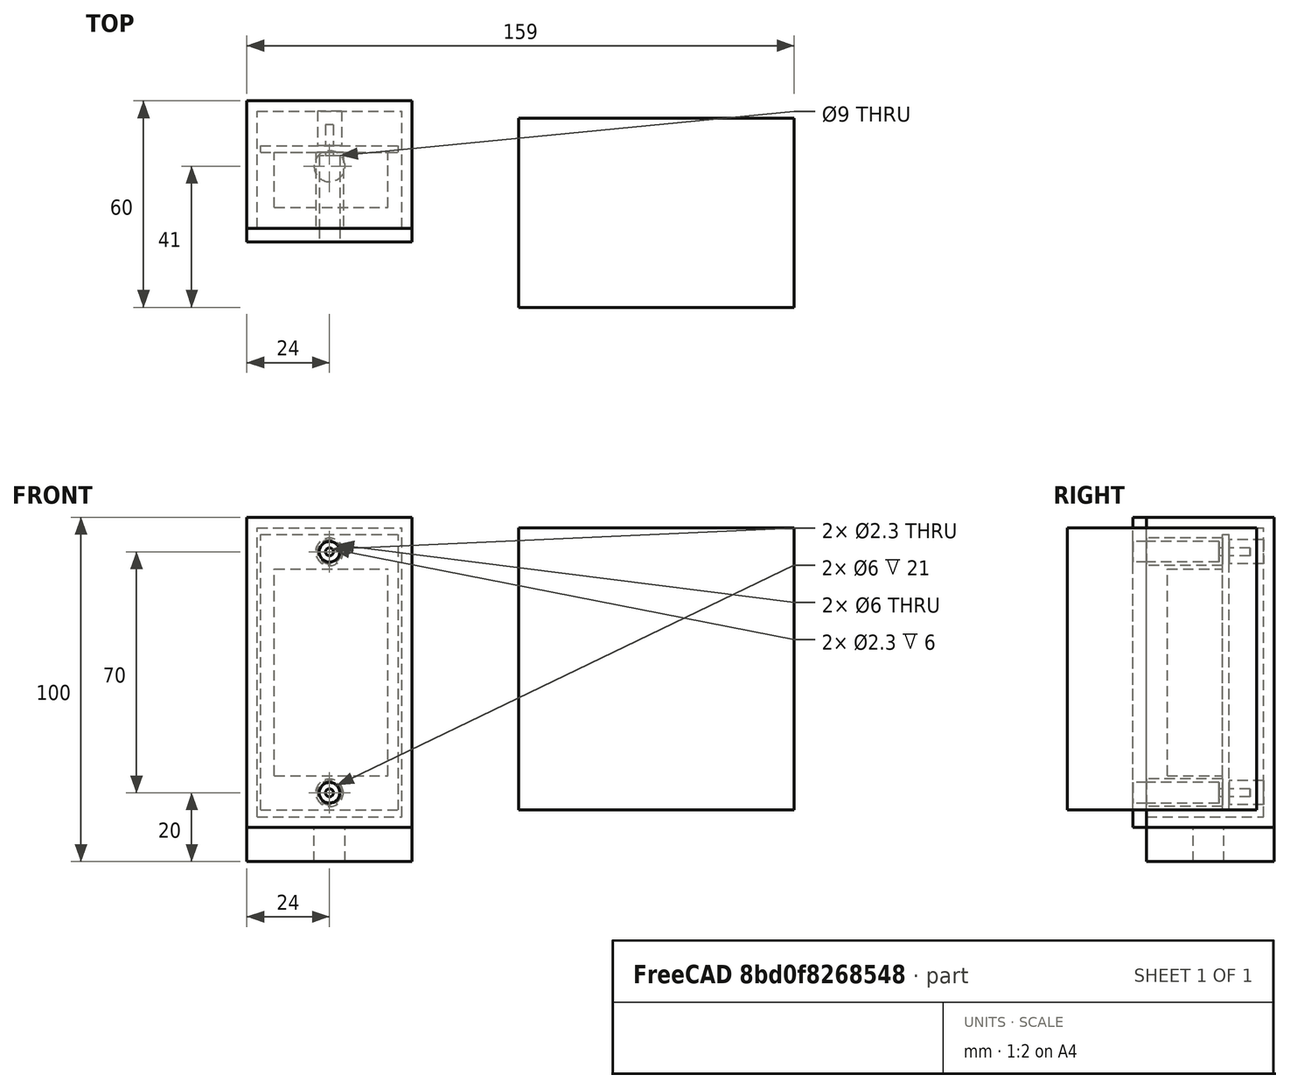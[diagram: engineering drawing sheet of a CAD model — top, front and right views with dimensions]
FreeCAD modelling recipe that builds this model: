
FCSTD DOCUMENT  (FreeCAD 0.15R4671 (Git))
Label: Sense_Beam Basic Enclosure
License: All rights reserved
LicenseURL: http://en.wikipedia.org/wiki/All_rights_reserved
objects: Part::Cylinder×13, Part::MultiFuse×8, Part::Box×7, Part::Cut×6
note: 34 computed .brp shape members not serialized (recipe doc carries the construction recipe); baked Part::Feature solids carry a one-line shape summary decoded from their .brp

FEATURE [Part::Cylinder] Cylinder002  label="PCB Mount1"
  Angle = 360
  Height = 10
  Placement = pos=(0,12,75) rot=(1,0,0;1.5708rad)
  Radius = 3.5
FEATURE [Part::Cylinder] Cylinder003  label="PCB Mount2"
  Angle = 360
  Height = 10
  Placement = pos=(0,12,5) rot=(1,0,0;1.5708rad)
  Radius = 3.5
FEATURE [Part::Cylinder] Cylinder004  label="PCB Mount_cut1"
  Angle = 360
  Height = 6
  Placement = pos=(0,8,75) rot=(1,0,0;1.5708rad)
  Radius = 1.15
FEATURE [Part::Cylinder] Cylinder005  label="PCB Mount_cut2"
  Angle = 360
  Height = 6
  Placement = pos=(0,8,5) rot=(1,0,0;1.5708rad)
  Radius = 1.15
FEATURE [Part::Box] Box  label="PCB"
  Height = 80
  Length = 40
  Placement = pos=(-20,0,0) rot=(0,0,1;0rad)
  Width = 2
FEATURE [Part::Box] Box001  label="AA Battery"
  Height = 60
  Length = 33
  Placement = pos=(-16,-16,10) rot=(0,0,1;0rad)
  Width = 16
FEATURE [Part::Box] Box002  label="G366"
  Height = 82
  Length = 80
  Placement = pos=(55,-45,0) rot=(0,0,1;0rad)
  Width = 55
FEATURE [Part::Cylinder] Cylinder010  label="Back_Mount_cut1"
  Angle = 360
  Height = 22
  Placement = pos=(0,0,75) rot=(1,0,0;1.5708rad)
  Radius = 4
FEATURE [Part::Cylinder] Cylinder011  label="Back_Mount_cut2"
  Angle = 360
  Height = 22
  Placement = pos=(0,0,5) rot=(1,0,0;1.5708rad)
  Radius = 4
FEATURE [Part::Cylinder] Cylinder012  label="PCB Mount_cut2+1"
  Angle = 360
  Height = 6
  Placement = pos=(0,5,5) rot=(1,0,0;1.5708rad)
  Radius = 1.15
FEATURE [Part::Cylinder] Cylinder013  label="PCB Mount_cut1+1"
  Angle = 360
  Height = 6
  Placement = pos=(0,5,75) rot=(1,0,0;1.5708rad)
  Radius = 1.15
FEATURE [Part::MultiFuse] Fusion003
  Shapes = -> [Cylinder004,Cylinder005]
FEATURE [Part::Box] Box003  label="Cube"
  Height = 90
  Length = 48
  Placement = pos=(-24,-22,-5) rot=(0,0,1;0rad)
  Width = 37
FEATURE [Part::Box] Box004  label="Cube001"
  Height = 84
  Length = 42
  Placement = pos=(-21,-22,-2) rot=(0,0,1;0rad)
  Width = 34
FEATURE [Part::Cut] Cut
  Base = -> Box003
  Tool = -> Box004
FEATURE [Part::Box] Box005  label="Back_Cover"
  Height = 90
  Length = 48
  Placement = pos=(-24,-26,-5) rot=(0,0,1;0rad)
  Width = 4
FEATURE [Part::Cylinder] Cylinder  label="PCB Mount_cut1+2"
  Angle = 360
  Height = 22
  Placement = pos=(0,-1,75) rot=(1,0,0;1.5708rad)
  Radius = 3
FEATURE [Part::Cylinder] Cylinder014  label="PCB Mount_cut2+2"
  Angle = 360
  Height = 22
  Placement = pos=(0,-1,5) rot=(1,0,0;1.5708rad)
  Radius = 3
FEATURE [Part::MultiFuse] Fusion
  Shapes = -> [Cylinder013,Cylinder]
FEATURE [Part::MultiFuse] Fusion004
  Shapes = -> [Cylinder012,Cylinder014]
FEATURE [Part::Cut] Cut001  label="Back M 2"
  Base = -> Cylinder011
  Tool = -> Fusion004
FEATURE [Part::Cut] Cut002  label="Back M 1"
  Base = -> Cylinder010
  Tool = -> Fusion
FEATURE [Part::MultiFuse] Fusion005
  Shapes = -> [Cut002,Cut001]
FEATURE [Part::Cylinder] Cylinder015  label="Back_Mount_cut003"
  Angle = 360
  Height = 10
  Placement = pos=(0,-16,75) rot=(1,0,0;1.5708rad)
  Radius = 3
FEATURE [Part::Cylinder] Cylinder016  label="Back_Mount_cut004"
  Angle = 360
  Height = 10
  Placement = pos=(0,-16,5) rot=(1,0,0;1.5708rad)
  Radius = 3
FEATURE [Part::MultiFuse] Fusion006
  Shapes = -> [Cylinder015,Cylinder016]
FEATURE [Part::Cut] Cut003
  Base = -> Box005
  Tool = -> Fusion006
FEATURE [Part::MultiFuse] Fusion007  label="Back"
  Shapes = -> [Fusion005,Cut003]
FEATURE [Part::MultiFuse] Fusion008
  Shapes = -> [Cylinder002,Cylinder003]
FEATURE [Part::Cut] Cut004
  Base = -> Fusion008
  Tool = -> Fusion003
FEATURE [Part::MultiFuse] Fusion009  label="Front"
  Shapes = -> [Cut,Cut004]
FEATURE [Part::Box] Box006  label="Base"
  Height = 10
  Length = 48
  Placement = pos=(-24,-22,-15) rot=(0,0,1;0rad)
  Width = 37
FEATURE [Part::Cylinder] Cylinder017  label="Cylinder"
  Angle = 360
  Height = 10
  Placement = pos=(0,-4,-15) rot=(0,0,1;0rad)
  Radius = 4.5
FEATURE [Part::Cut] Cut005  label="BasewCut"
  Base = -> Box006
  Tool = -> Cylinder017
